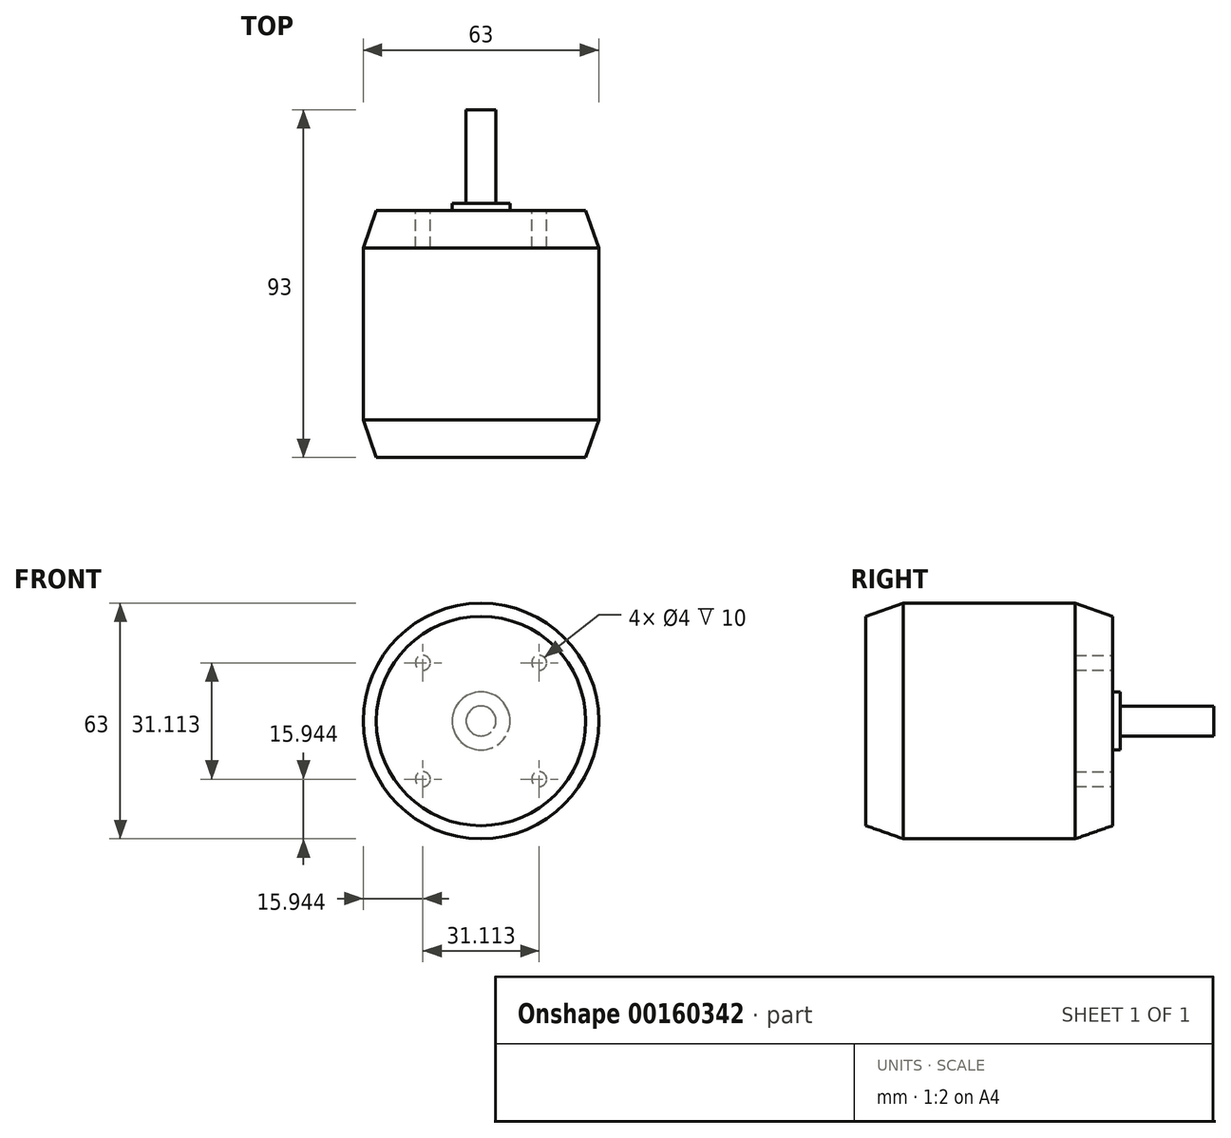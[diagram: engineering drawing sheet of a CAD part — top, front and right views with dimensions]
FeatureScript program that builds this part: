
annotation { "Feature Type Name" : "Feature", "Feature Type Description" : "" }
export const myFeature = defineFeature(function(context is Context, id is Id, definition is map)
    precondition{}
    {
        {
            var Q0;
            Q0=qCreatedBy(makeId("Front.planeOp"),FACE);
            var sketch = newSketch(context, id + "F0", { "sketchPlane" : qUnion([Q0])});
            skCircle(sketch, "E0", {"center": v(0, 0) * mm, "radius": 31.5 * mm});
            skCircle(sketch, "E1", {"center": v(0, 0) * mm, "radius": 4 * mm});
            skCircle(sketch, "E2", {"center": v(0, 0) * mm, "radius": 22 * mm, "construction": true});
            skLineSegment(sketch, "E3", {"start": v(0, 0) * mm, "end": v(-15.56, 15.56) * mm, "construction": true});
            skCircle(sketch, "E4", {"center": v(-15.56, 15.56) * mm, "radius": 2 * mm});
            skCircle(sketch, "E5.1.0", {"center": v(-15.56, -15.56) * mm, "radius": 2 * mm});
            skCircle(sketch, "E5.2.0", {"center": v(15.56, -15.56) * mm, "radius": 2 * mm});
            skCircle(sketch, "E6.1.3.0", {"center": v(15.56, 15.56) * mm, "radius": 2 * mm});
            skSolve(sketch);
        }
        {
            var Q0;
            Q0=makeQuery(id+"F0.imprint","IMPRINT",FACE,{"disambiguationData":[TD([[makeQuery(id+"F0.imprint","IMPRINT",EDGE,{"derivedFrom":sQuery(id+"F0.wireOp",EDGE,"E0")}),1.0]])]});
            var Q1;
            Q1=makeQuery(id+"F0.imprint","IMPRINT",FACE,{"disambiguationData":[TD([[makeQuery(id+"F0.imprint","IMPRINT",EDGE,{"derivedFrom":sQuery(id+"F0.wireOp",EDGE,"E1")}),1.0]])]});
            var Q2;
            Q2=makeQuery(id+"F0.imprint","IMPRINT",FACE,{"disambiguationData":[TD([[makeQuery(id+"F0.imprint","IMPRINT",EDGE,{"derivedFrom":sQuery(id+"F0.wireOp",EDGE,"E6.1.3.0")}),1.0]])]});
            var Q3;
            Q3=makeQuery(id+"F0.imprint","IMPRINT",FACE,{"disambiguationData":[TD([[makeQuery(id+"F0.imprint","IMPRINT",EDGE,{"derivedFrom":sQuery(id+"F0.wireOp",EDGE,"E4")}),1.0]])]});
            var Q4;
            Q4=makeQuery(id+"F0.imprint","IMPRINT",FACE,{"disambiguationData":[TD([[makeQuery(id+"F0.imprint","IMPRINT",EDGE,{"derivedFrom":sQuery(id+"F0.wireOp",EDGE,"E5.1.0")}),1.0]])]});
            var Q5;
            Q5=makeQuery(id+"F0.imprint","IMPRINT",FACE,{"disambiguationData":[TD([[makeQuery(id+"F0.imprint","IMPRINT",EDGE,{"derivedFrom":sQuery(id+"F0.wireOp",EDGE,"E5.2.0")}),1.0]])]});
            extrude(context, id + "F1", {"entities" : qUnion([Q0, Q1, Q2, Q3, Q4, Q5]), "depth" : 66 * mm, "offsetDistance" : 25 * mm});
        }
        {
            var Q0;
            Q0=makeQuery(id+"F0.imprint","IMPRINT",FACE,{"disambiguationData":[TD([[makeQuery(id+"F0.imprint","IMPRINT",EDGE,{"derivedFrom":sQuery(id+"F0.wireOp",EDGE,"E1")}),1.0]])]});
            extrude(context, id + "F2", {"entities" : qUnion([Q0]), "operationType" : NewBodyOperationType.ADD, "oppositeDirection" : true, "depth" : 27 * mm});
        }
        {
            var Q0;
            Q0=makeQuery(id+"F0.imprint","IMPRINT",FACE,{"disambiguationData":[TD([[makeQuery(id+"F0.imprint","IMPRINT",EDGE,{"derivedFrom":sQuery(id+"F0.wireOp",EDGE,"E6.1.3.0")}),1.0]])]});
            var Q1;
            Q1=makeQuery(id+"F0.imprint","IMPRINT",FACE,{"disambiguationData":[TD([[makeQuery(id+"F0.imprint","IMPRINT",EDGE,{"derivedFrom":sQuery(id+"F0.wireOp",EDGE,"E4")}),1.0]])]});
            var Q2;
            Q2=makeQuery(id+"F0.imprint","IMPRINT",FACE,{"disambiguationData":[TD([[makeQuery(id+"F0.imprint","IMPRINT",EDGE,{"derivedFrom":sQuery(id+"F0.wireOp",EDGE,"E5.2.0")}),1.0]])]});
            var Q3;
            Q3=makeQuery(id+"F0.imprint","IMPRINT",FACE,{"disambiguationData":[TD([[makeQuery(id+"F0.imprint","IMPRINT",EDGE,{"derivedFrom":sQuery(id+"F0.wireOp",EDGE,"E5.1.0")}),1.0]])]});
            extrude(context, id + "F3", {"entities" : qUnion([Q0, Q1, Q2, Q3]), "operationType" : NewBodyOperationType.REMOVE, "depth" : 10 * mm});
        }
        {
            var Q0;
            Q0=makeQuery(id+"F1.opExtrude","CAP_EDGE",EDGE,{"disambiguationData":[OSD([sQuery(id+"F0.wireOp",EDGE,"E0")])],"isStart":true});
            chamfer(context, id + "F4", {"entities" : qUnion([Q0]), "chamferType" : ChamferType.TWO_OFFSETS, "width1" : 10 * mm, "oppositeDirection" : false, "width2" : 3.5 * mm, "tangentPropagation" : true});
        }
        {
            var Q0;
            Q0=makeQuery(id+"F1.opExtrude","CAP_EDGE",EDGE,{"disambiguationData":[OSD([sQuery(id+"F0.wireOp",EDGE,"E0")])],"isStart":false});
            chamfer(context, id + "F5", {"entities" : qUnion([Q0]), "chamferType" : ChamferType.TWO_OFFSETS, "width1" : 3.5 * mm, "oppositeDirection" : false, "width2" : 10 * mm, "tangentPropagation" : true});
        }
        {
            var Q0;
            Q0=makeQuery(id+"F1.opExtrude","CAP_FACE",FACE,{"disambiguationData":[OSD([sQuery(id+"F0.wireOp",EDGE,"E0")])],"isStart":true});
            var sketch = newSketch(context, id + "F6", { "sketchPlane" : qUnion([Q0])});
            skCircle(sketch, "E7", {"center": v(0, 0) * mm, "radius": 7.75 * mm});
            skSolve(sketch);
        }
        {
            var Q0;
            Q0=makeQuery(id+"F6.imprint","IMPRINT",FACE,{"disambiguationData":[TD([[makeQuery(id+"F6.imprint","IMPRINT",EDGE,{"derivedFrom":sQuery(id+"F6.wireOp",EDGE,"E7")}),1.0]])]});
            extrude(context, id + "F7", {"entities" : qUnion([Q0]), "operationType" : NewBodyOperationType.ADD, "depth" : 2 * mm, "offsetDistance" : 25 * mm});
        }
    });
